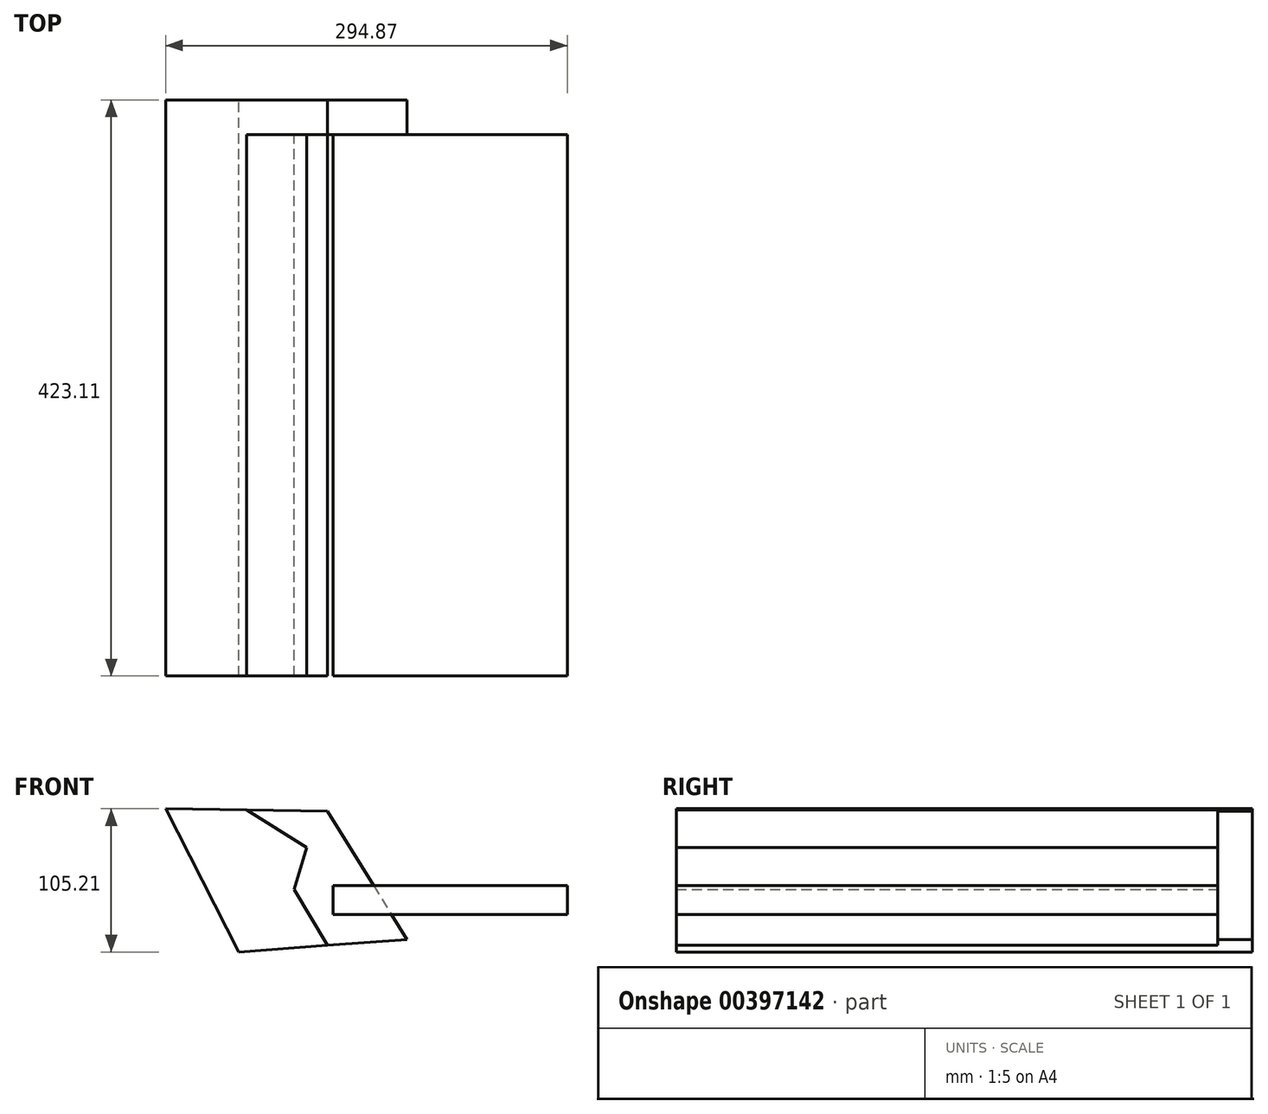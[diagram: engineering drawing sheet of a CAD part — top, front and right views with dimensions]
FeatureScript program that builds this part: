
annotation { "Feature Type Name" : "Feature", "Feature Type Description" : "" }
export const myFeature = defineFeature(function(context is Context, id is Id, definition is map)
    precondition{}
    {
        {
            var Q0;
            Q0=qCreatedBy(makeId("Front.planeOp"),FACE);
            var sketch = newSketch(context, id + "F0", { "sketchPlane" : qUnion([Q0])});
            skLineSegment(sketch, "E0", {"start": v(98.72, -96.3) * mm, "end": v(157, -190.46) * mm});
            skLineSegment(sketch, "E1", {"start": v(157, -190.46) * mm, "end": v(33.61, -199.65) * mm});
            skLineSegment(sketch, "E2", {"start": v(33.61, -199.65) * mm, "end": v(-20.1, -94.44) * mm});
            skLineSegment(sketch, "E3", {"start": v(-20.1, -94.44) * mm, "end": v(98.72, -96.3) * mm});
            skLineSegment(sketch, "E4", {"start": v(100.76, -154.36) * mm, "end": v(100.76, -163.63) * mm});
            skSolve(sketch);
        }
        {
            var Q0;
            Q0=makeQuery(id+"F0.imprint","IMPRINT",FACE,{"disambiguationData":[TD([[makeQuery(id+"F0.imprint","IMPRINT",EDGE,{"derivedFrom":sQuery(id+"F0.wireOp",EDGE,"E0")}),-1.0]])]});
            extrude(context, id + "F1", {"entities" : qUnion([Q0]), "depth" : 25.4 * mm});
        }
        {
            var Q0;
            Q0=makeQuery(id+"F1.opExtrude","CAP_FACE",FACE,{"disambiguationData":[OSD([sQuery(id+"F0.wireOp",EDGE,"E0"),sQuery(id+"F0.wireOp",EDGE,"E1"),sQuery(id+"F0.wireOp",EDGE,"E2"),sQuery(id+"F0.wireOp",EDGE,"E3")])],"isStart":false});
            var sketch = newSketch(context, id + "F2", { "sketchPlane" : qUnion([Q0])});
            skLineSegment(sketch, "E5", {"start": v(98.86, -194.79) * mm, "end": v(39.31, -95.37) * mm});
            skLineSegment(sketch, "E6", {"start": v(39.31, -95.37) * mm, "end": v(83.46, -122.78) * mm});
            skLineSegment(sketch, "E7", {"start": v(83.46, -122.78) * mm, "end": v(69.09, -170.73) * mm});
            skPoint(sketch, "E7.endSnap0", {"position": v(69.09, -145.08) * mm});
            skLineSegment(sketch, "E8", {"start": v(69.09, -170.73) * mm, "end": v(98.86, -194.79) * mm});
            skLineSegment(sketch, "E9.bottom", {"start": v(274.78, -172.07) * mm, "end": v(102.98, -172.07) * mm});
            skLineSegment(sketch, "E9.top", {"start": v(274.78, -150.97) * mm, "end": v(102.98, -150.97) * mm});
            skLineSegment(sketch, "E9.left", {"start": v(274.78, -172.07) * mm, "end": v(274.78, -150.97) * mm});
            skLineSegment(sketch, "E9.right", {"start": v(102.98, -172.07) * mm, "end": v(102.98, -150.97) * mm});
            skSolve(sketch);
        }
        {
            var Q0;
            {var subQ6=sQuery(id+"F2.wireOp",EDGE,"E8");Q0=makeQuery(id+"F2.imprint","IMPRINT",FACE,{"disambiguationData":[TD([[makeQuery(id+"F2.imprint","IMPRINT",EDGE,{"derivedFrom":subQ6}),-1.0]])]});}
            var Q1;
            Q1 = qSketchRegion(id + "F2", true);
            extrude(context, id + "F3", {"entities" : qUnion([Q0, Q1]), "operationType" : NewBodyOperationType.ADD, "depth" : 397.7 * mm});
        }
    });
